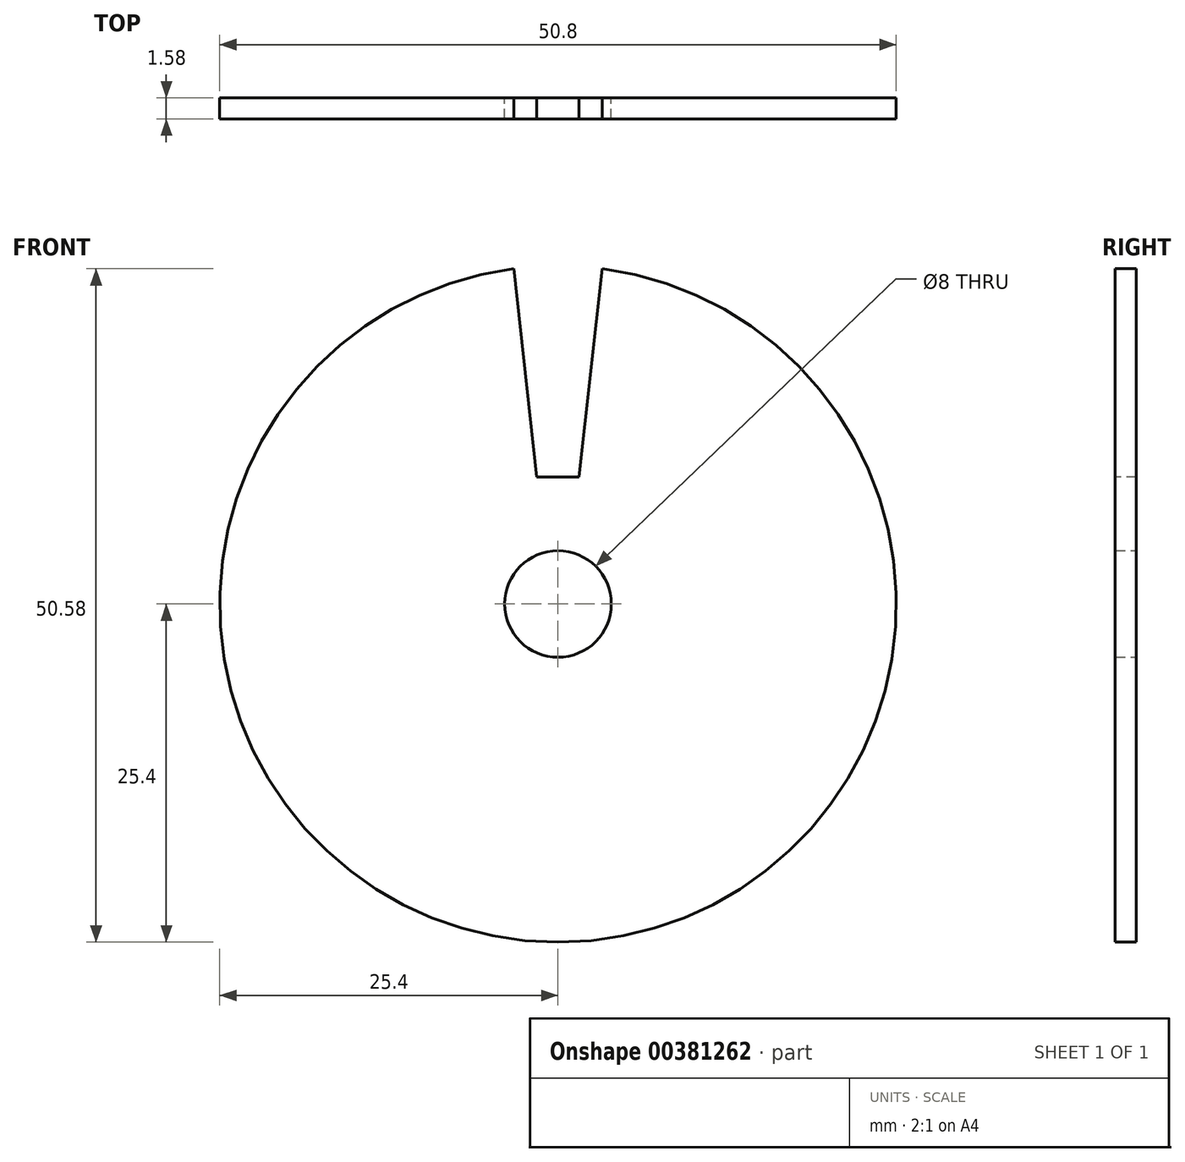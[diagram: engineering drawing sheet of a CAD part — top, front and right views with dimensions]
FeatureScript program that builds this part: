
annotation { "Feature Type Name" : "Feature", "Feature Type Description" : "" }
export const myFeature = defineFeature(function(context is Context, id is Id, definition is map)
    precondition{}
    {
        {
            var Q0;
            Q0=qCreatedBy(makeId("Front.planeOp"),FACE);
            var sketch = newSketch(context, id + "F0", { "sketchPlane" : qUnion([Q0])});
            skCircle(sketch, "E0", {"center": v(0, 0) * mm, "radius": 25.4 * mm});
            skCircle(sketch, "E1", {"center": v(0, 0) * mm, "radius": 4 * mm});
            skSolve(sketch);
        }
        {
            var Q0;
            Q0 = qSketchRegion(id + "F0", true);
            extrude(context, id + "F1", {"entities" : qUnion([Q0]), "endBound" : BoundingType.SYMMETRIC, "depth" : 1.59 * mm});
        }
        {
            var Q0;
            Q0=makeQuery(id+"F1.opExtrude","CAP_FACE",FACE,{"disambiguationData":[OSD([sQuery(id+"F0.wireOp",EDGE,"E0"),sQuery(id+"F0.wireOp",EDGE,"E1")])],"isStart":false});
            var sketch = newSketch(context, id + "F2", { "sketchPlane" : qUnion([Q0])});
            skLineSegment(sketch, "E2.top", {"start": v(1.59, 9.53) * mm, "end": v(-1.59, 9.53) * mm});
            skPoint(sketch, "E2.middle", {"position": v(0, 55.57) * mm});
            skLineSegment(sketch, "E3", {"start": v(-3.32, 25.18) * mm, "end": v(0, 29.9) * mm});
            skLineSegment(sketch, "E4", {"start": v(0, 29.9) * mm, "end": v(3.32, 25.18) * mm});
            skPoint(sketch, "E5.orphan", {"position": v(0, 9.53) * mm});
            skPoint(sketch, "E2.right.start.orphan", {"position": v(-1.59, 101.62) * mm});
            skPoint(sketch, "E2.left.start.orphan", {"position": v(1.59, 101.62) * mm});
            skLineSegment(sketch, "E6", {"start": v(-1.59, 9.53) * mm, "end": v(-3.32, 25.18) * mm});
            skLineSegment(sketch, "E7", {"start": v(1.59, 9.52) * mm, "end": v(3.32, 25.18) * mm});
            skLineSegment(sketch, "E8", {"start": v(0, 0) * mm, "end": v(0, 9.53) * mm, "construction": true});
            skSolve(sketch);
        }
        {
            var Q0;
            Q0 = qSketchRegion(id + "F2", true);
            extrude(context, id + "F3", {"entities" : qUnion([Q0]), "operationType" : NewBodyOperationType.REMOVE, "oppositeDirection" : true, "depth" : 25.4 * mm});
        }
    });
